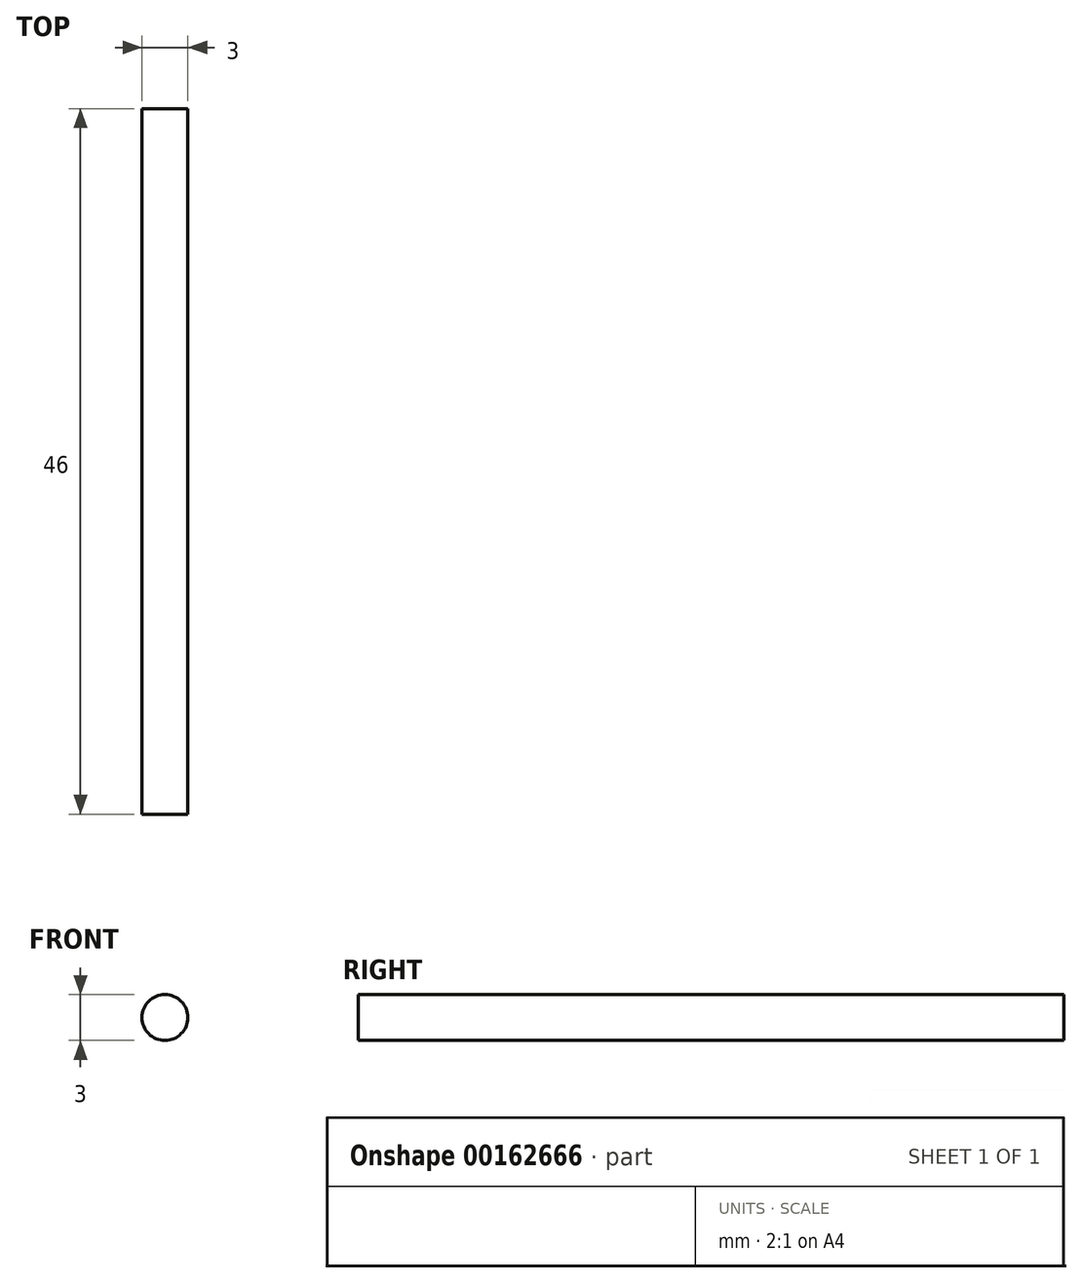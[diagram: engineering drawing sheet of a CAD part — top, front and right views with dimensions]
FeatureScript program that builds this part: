
annotation { "Feature Type Name" : "Feature", "Feature Type Description" : "" }
export const myFeature = defineFeature(function(context is Context, id is Id, definition is map)
    precondition{}
    {
        {
            var Q0;
            Q0=qCreatedBy(makeId("Front.planeOp"),FACE);
            var sketch = newSketch(context, id + "F0", { "sketchPlane" : qUnion([Q0])});
            skCircle(sketch, "E0", {"center": v(0, 0) * mm, "radius": 1.5 * mm});
            skSolve(sketch);
        }
        {
            var Q0;
            Q0 = qSketchRegion(id + "F0", true);
            extrude(context, id + "F1", {"entities" : qUnion([Q0]), "depth" : 46 * mm, "offsetDistance" : 25 * mm});
        }
    });
